# Revit family: WVA-10
name_source: partatom
category: Mechanical Equipment
revit_build: Autodesk Revit MEP 2014 (Build: 20140709_2115(x64)
units: mm (PartAtom-declared; Revit-internal decimal feet)

## types (1)
- WVA-10
    A = 27 1/2"
    ApproximateShipmentWeight = 1000 lbs
    ArrayRadius = 12"
    B = 65"
    BottomExtrusionHeight = 3/4"
    BottomRevolveHeight = 7 1/8"
    C = 37 1/2"
    CouplingHeight = 10 1/8"
    CylindarDia = 19 1/4"
    CylinderHalfLength = 13 3/4"
    CylinderHeight = 50 3/4"
    D = 32 1/2"
    DrainExtrusionPosition = 2 3/8"
    Height1 = 2 1/8"
    Height2 = 3/8"
    HookDiameter = 5/8"
    HookDistance = 5 3/8"
    HookTopDistance = 7/8"
    HookWidth = 1 7/8"
    LeftHookDistance = 3/8"
    Manufacturer = Wessels Company
    MaximumFlow = 1440 GPM
    MaximumOperatingPressure = 125 PSIG
    MaximumOperatingTemperature = 240°F
    Model = WVA-10
    NumberOfArray = 9
    PartNumber = 72080100
    PipeConnectorDiameter = 10"
    PipeDiameter = 10 3/4"
    RevolveRadius = 9 5/8"
    RingDistance = 12 3/4"
    SideDrainExtrusion = 1 3/4"
    SideFlangeStep1 = 12"
    SideFlangeStep2 = 16"
    SideFlangeThickness = 1 1/8"
    SideFlangeThickness1 = 3/4"
    Step1Diameter = 1 1/2"
    Step2Diameter = 3"
    Step3Diameter = 5"
    Step4Diameter = 7"
    Step5Diameter = 6"
    TopExtrusionDiameter = 3"
    TotalHeight = 8 7/8"
    URL = http://westank.com

## geometry (parser evidence)
native form markers: Extrusion x4, Revolve x2, Sweep x5
no freeform markers — native parametric forms only
